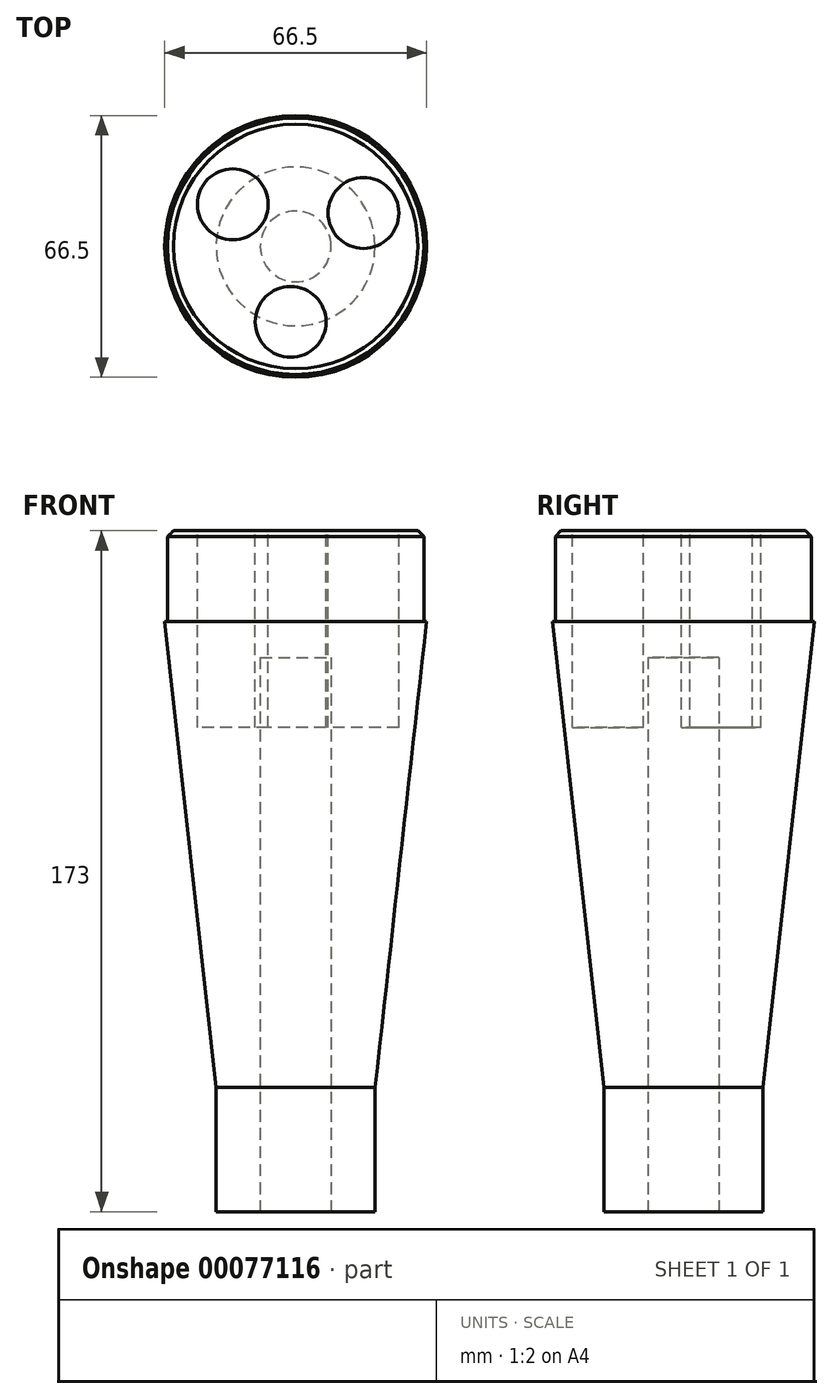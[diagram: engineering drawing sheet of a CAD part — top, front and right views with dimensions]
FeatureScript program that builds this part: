
annotation { "Feature Type Name" : "Feature", "Feature Type Description" : "" }
export const myFeature = defineFeature(function(context is Context, id is Id, definition is map)
    precondition{}
    {
        {
            var Q0;
            Q0=qCreatedBy(makeId("Front.planeOp"),FACE);
            var sketch = newSketch(context, id + "F0", { "sketchPlane" : qUnion([Q0])});
            skLineSegment(sketch, "E0", {"start": v(-32.55, 66.27) * mm, "end": v(-32.55, 43.27) * mm});
            skLineSegment(sketch, "E1", {"start": v(-32.55, 43.27) * mm, "end": v(-33.25, 43.27) * mm});
            skLineSegment(sketch, "E2", {"start": v(-33.25, 43.27) * mm, "end": v(-20.2, -75.18) * mm});
            skLineSegment(sketch, "E3", {"start": v(-20.2, -75.18) * mm, "end": v(-20.2, -106.73) * mm});
            skLineSegment(sketch, "E4", {"start": v(-20.2, -106.73) * mm, "end": v(0, -106.73) * mm});
            skLineSegment(sketch, "E5", {"start": v(-32.55, 66.27) * mm, "end": v(0, 66.27) * mm});
            skLineSegment(sketch, "E6", {"start": v(0, 94.78) * mm, "end": v(0, -99.97) * mm, "construction": true});
            skLineSegment(sketch, "E7", {"start": v(0, 66.27) * mm, "end": v(0, -106.73) * mm});
            skPoint(sketch, "E8.start.orphan", {"position": v(-20.8, -69.73) * mm});
            skPoint(sketch, "E9.orphan", {"position": v(-20.2, -69.73) * mm});
            skSolve(sketch);
        }
        {
            var Q0;
            Q0=makeQuery(id+"F0.imprint","IMPRINT",FACE,{"disambiguationData":[TD([[makeQuery(id+"F0.imprint","IMPRINT",EDGE,{"derivedFrom":sQuery(id+"F0.wireOp",EDGE,"E0")}),1.0]])]});
            var Q1;
            Q1=sQuery(id+"F0.wireOp",EDGE,"E6");
            revolve(context, id + "F1", {"entities" : qUnion([Q0]), "axis" : qUnion([Q1]), "revolveType" : RevolveType.FULL});
        }
        {
            var Q0;
            Q0=makeQuery(id+"F1.opRevolve","SWEPT_EDGE",EDGE,{"disambiguationData":[OSD([sQuery(id+"F0.wireOp",EDGE,"E0"),sQuery(id+"F0.wireOp",EDGE,"E5")])]});
            chamfer(context, id + "F2", {"entities" : qUnion([Q0]), "width" : 1.5 * mm, "tangentPropagation" : true});
        }
        {
            var Q0;
            Q0=qCreatedBy(makeId("Right.planeOp"),FACE);
            var sketch = newSketch(context, id + "F3", { "sketchPlane" : qUnion([Q0])});
            skLineSegment(sketch, "E10.top", {"start": v(0, -120) * mm, "end": v(-9, -120) * mm});
            skLineSegment(sketch, "E10.left", {"start": v(0, 0) * mm, "end": v(0, -120) * mm});
            skLineSegment(sketch, "E10.right", {"start": v(-9, 0) * mm, "end": v(-9, -120) * mm});
            skLineSegment(sketch, "E11.top", {"start": v(0, 34.12) * mm, "end": v(-9, 34.12) * mm});
            skLineSegment(sketch, "E11.left", {"start": v(0, 0) * mm, "end": v(0, 34.12) * mm});
            skLineSegment(sketch, "E11.right", {"start": v(-9, 0) * mm, "end": v(-9, 34.12) * mm});
            skSolve(sketch);
        }
        {
            var Q0;
            Q0=makeQuery(id+"F3.imprint","IMPRINT",FACE,{"disambiguationData":[TD([[makeQuery(id+"F3.imprint","IMPRINT",EDGE,{"derivedFrom":sQuery(id+"F3.wireOp",EDGE,"E10.top")}),-1.0]])]});
            var Q1;
            Q1=sQuery(id+"F0.wireOp",EDGE,"E7");
            revolve(context, id + "F4", {"operationType" : NewBodyOperationType.REMOVE, "entities" : qUnion([Q0]), "axis" : qUnion([Q1]), "revolveType" : RevolveType.FULL, "oppositeDirection" : true});
        }
        {
            var Q0;
            Q0=makeQuery(id+"F1.opRevolve","SWEPT_FACE",FACE,{"disambiguationData":[OSD([sQuery(id+"F0.wireOp",EDGE,"E5")])]});
            var sketch = newSketch(context, id + "F5", { "sketchPlane" : qUnion([Q0])});
            skCircle(sketch, "E12", {"center": v(-15.97, 10.69) * mm, "radius": 9 * mm});
            skCircle(sketch, "E13.1.0", {"center": v(-1.27, -19.18) * mm, "radius": 9 * mm});
            skCircle(sketch, "E13.2.0", {"center": v(17.24, 8.49) * mm, "radius": 9 * mm});
            skPoint(sketch, "E13.center", {"position": v(0, 0) * mm});
            skSolve(sketch);
        }
        {
            var Q0;
            Q0=makeQuery(id+"F5.imprint","IMPRINT",FACE,{"disambiguationData":[TD([[makeQuery(id+"F5.imprint","IMPRINT",EDGE,{"derivedFrom":sQuery(id+"F5.wireOp",EDGE,"E12")}),1.0]])]});
            var Q1;
            Q1=makeQuery(id+"F5.imprint","IMPRINT",FACE,{"disambiguationData":[TD([[makeQuery(id+"F5.imprint","IMPRINT",EDGE,{"derivedFrom":sQuery(id+"F5.wireOp",EDGE,"E13.2.0")}),1.0]])]});
            var Q2;
            Q2=makeQuery(id+"F5.imprint","IMPRINT",FACE,{"disambiguationData":[TD([[makeQuery(id+"F5.imprint","IMPRINT",EDGE,{"derivedFrom":sQuery(id+"F5.wireOp",EDGE,"E13.1.0")}),1.0]])]});
            extrude(context, id + "F6", {"entities" : qUnion([Q0, Q1, Q2]), "operationType" : NewBodyOperationType.REMOVE, "depth" : -50 * mm, "offsetDistance" : 25 * mm});
        }
    });
